# Revit family: ADB Armoire Cuiseur à pâtes électrique CME 410 CP
name_source: partatom
category: Equipement spécialisé
units: mm (PartAtom-declared; Revit-internal decimal feet)

## family parameters
Basée sur le plan de construction = Non
Conserver l'orientation des annotations = Non
Cote de connecteur circulaire = Utiliser le diamètre
Couper avec des vides une fois chargée = Non
Numéro OmniClass = 23.40.40.14.17.11
Partagée = Non
Repère de localisation dans la pièce = Non
Titre OmniClass = Cookers, Ovens, Stoves
Toujours verticalement = Oui
Type d'élément = Normal

## types (1)
- CME 410 CP
    C = 200 mm  [stored 0.656168 ft]
    Commentaires du type = Gamme Ambassade - Armoires - Cuiseur à pâtes
    D = 765 mm  [stored 2.50984 ft]
    Description = Cuiseur à pâtes électrique
    Diamètre de Raccordement Eau Froide = 27.00 mm
    Diamètre de Raccordement Evacuation = 17.00 mm
    Débit Eau Froide = 0.2 L/s
    Elévation par défaut = 0 mm  [stored 0 ft]
    Fabricant = Société Industrielle de Lacanche
    Modèle = CME 410 CP
    Remarques Plomberie = 27/20
    Table = CME410 CP
    URL = https://www.ambassade-de-bourgogne.com
    URL catalogue = https://www.ambassade-de-bourgogne.com

note: [stored X ft] marks values corroborated as IEEE doubles in the binary element streams (Revit-internal decimal feet)
